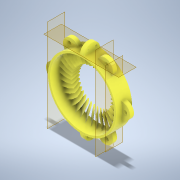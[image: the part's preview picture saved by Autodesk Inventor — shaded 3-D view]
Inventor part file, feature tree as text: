
AUTODESK INVENTOR PART (.ipt)
format: ipt  version: 2021.2 (Build 252289000, 289)  size: 988,160 bytes
history: native  units: in
note: dims shown in document units (in); Inventor stores cm internally (conversion verified against a paired STEP export)
features: sketch x9, extrude x8, plane x4, pattern_circular x3, fillet x2, loft x1, other x1
ambient origin geometry x8: Origin, YZ Plane, XZ Plane, XY Plane, X Axis, Y Axis, Z Axis, Center Point
bodies: Solid1 (feature_tree)
feature tree (28):
  extrude  "Extrusion1"  Depth=4.25in
  plane  "Work Plane1"
  plane  "Work Plane2"
  extrude  "Extrusion3"  Depth=1.5in
  fillet  "Fillet1"  Radius=2.125in
  extrude  "Extrusion4"  TaperAngle=0.0deg  [1 undecoded]
  pattern_circular  "Circular Pattern2"  Count=2 Angle=360.0deg
  plane  "Work Plane3"
  extrude  "Extrusion5"  Depth=1.0in
  extrude  "Extrusion6"  Depth=0.25in
  fillet  "Fillet2"  Radius=0.5in
  extrude  "Extrusion7"  TaperAngle=0.0deg  [1 undecoded]
  pattern_circular  "Circular Pattern3"  [2 undecoded]
  extrude  "Extrusion8"  Depth=0.5in TaperAngle=0.0deg
  plane  "Work Plane4"
  loft  "Loft1"
  pattern_circular  "Circular Pattern5"  [2 undecoded]
  extrude  "Extrusion9"  Depth=0.2in
  sketch  "Sketch1"  dims[d0=4.0in d1=4.25in]
  sketch  "Sketch3"  dims[d2=1.0in d3=0.0in d4=1.5in d10=2.125in]
  sketch  "Sketch4"  dims[d11=0.25in d12=0.0in]
  sketch  "Sketch5"  dims[d13=0.5in d14=0.0in]
  sketch  "Sketch6"  dims[d15=0.5in]
  sketch  "Sketch7"  dims[d16=0.125in]
  sketch  "Sketch8"  dims[d17=0.2in]
  sketch  "Sketch9"  dims[d18=0.5in d19=0.0in d20=0.7874in d21=360.0deg]
  other  "Edges1"
  sketch  "Sketch10"  dims[d23=-2.125in d24=1.0in d25=0.25in d26=0.5in d27=0.0in d28=0.1in d29=0.0in d30=0.5in d31=0.0in d32=0.5in d33=0.25in d34=0.2in d35=0.5in d36=0.0in d37=2.3622in d38=360.0deg d40=0.25in d41=0.125in d42=0.25in d43=0.2in d49=0.5in d50=0.0312in d51=0.5in d52=0.0in d56=0.9in d57=0.0in d58=90.0deg d59=0.0in d60=90.0deg d61=14.1732in d62=360.0deg d64=2.2625in d65=0.0in d66=0.0777in]
note: 6 required parameter values undecoded (feature->parameter linkage not recoverable at this tier; creation-order binding heuristic only, values carry confidence <= 0.55)
